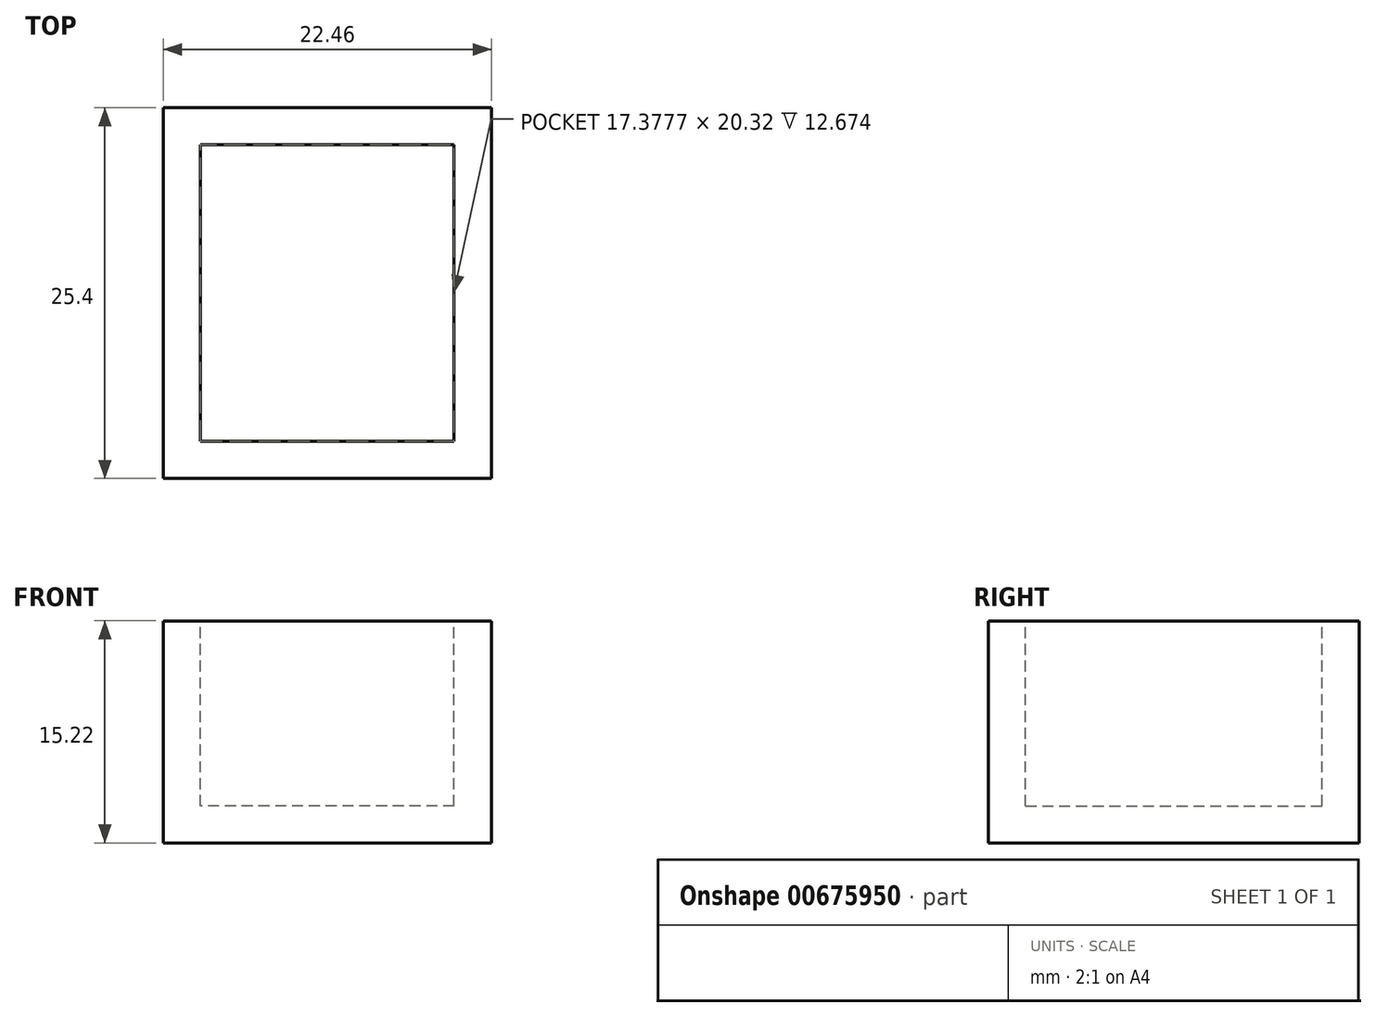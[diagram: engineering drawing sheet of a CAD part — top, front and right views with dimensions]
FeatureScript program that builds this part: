
annotation { "Feature Type Name" : "Feature", "Feature Type Description" : "" }
export const myFeature = defineFeature(function(context is Context, id is Id, definition is map)
    precondition{}
    {
        {
            var Q0;
            Q0=qCreatedBy(makeId("Front.planeOp"),FACE);
            var sketch = newSketch(context, id + "F0", { "sketchPlane" : qUnion([Q0])});
            skLineSegment(sketch, "E0.bottom", {"start": v(-62.4, -28.87) * mm, "end": v(62.4, -28.87) * mm});
            skLineSegment(sketch, "E0.top", {"start": v(-62.4, 28.87) * mm, "end": v(62.4, 28.87) * mm});
            skLineSegment(sketch, "E0.left", {"start": v(-62.4, -28.87) * mm, "end": v(-62.4, 28.87) * mm});
            skLineSegment(sketch, "E0.right", {"start": v(62.4, -28.87) * mm, "end": v(62.4, 28.87) * mm});
            skPoint(sketch, "E0.middle", {"position": v(0, 0) * mm});
            skLineSegment(sketch, "E1.bottom", {"start": v(-39.94, 13.65) * mm, "end": v(-84.86, 13.65) * mm});
            skLineSegment(sketch, "E1.top", {"start": v(-39.94, 44.08) * mm, "end": v(-84.86, 44.08) * mm});
            skLineSegment(sketch, "E1.left", {"start": v(-39.94, 13.65) * mm, "end": v(-39.94, 44.08) * mm});
            skLineSegment(sketch, "E1.right", {"start": v(-84.86, 13.65) * mm, "end": v(-84.86, 44.08) * mm});
            skPoint(sketch, "E1.middle", {"position": v(-62.4, 28.87) * mm});
            skLineSegment(sketch, "E2.bottom", {"start": v(40.45, 13.65) * mm, "end": v(84.35, 13.65) * mm});
            skLineSegment(sketch, "E2.top", {"start": v(40.45, 44.08) * mm, "end": v(84.35, 44.08) * mm});
            skLineSegment(sketch, "E2.left", {"start": v(40.45, 13.65) * mm, "end": v(40.45, 44.08) * mm});
            skLineSegment(sketch, "E2.right", {"start": v(84.35, 13.65) * mm, "end": v(84.35, 44.08) * mm});
            skPoint(sketch, "E2.middle", {"position": v(62.4, 28.87) * mm});
            skSolve(sketch);
        }
        {
            var Q0;
            {var subQ0=sQuery(id+"F0.wireOp",EDGE,"E0.left");var subQ1=sQuery(id+"F0.wireOp",EDGE,"E0.top");var subQ2=makeQuery(id+"F0.imprint","INTERSECT",VERTEX,{"derivedFrom":[subQ1,subQ0]});Q0=makeQuery(id+"F0.imprint","IMPRINT",FACE,{"disambiguationData":[TD([[makeQuery(id+"F0.imprint","IMPRINT",EDGE,{"disambiguationData":[TD([[subQ2,-1.0]])],"derivedFrom":subQ1}),-1.0]])]});}
            extrude(context, id + "F1", {"entities" : qUnion([Q0]), "depth" : 25.4 * mm, "offsetDistance" : 25.4 * mm});
        }
        {
            var Q0;
            Q0=makeQuery(id+"F1.opExtrude","SWEPT_FACE",FACE,{"disambiguationData":[OSD([sQuery(id+"F0.wireOp",EDGE,"E0.top")])]});
            shell(context, id + "F2", {"entities" : qUnion([Q0]), "thickness" : 2.54 * mm});
        }
    });
